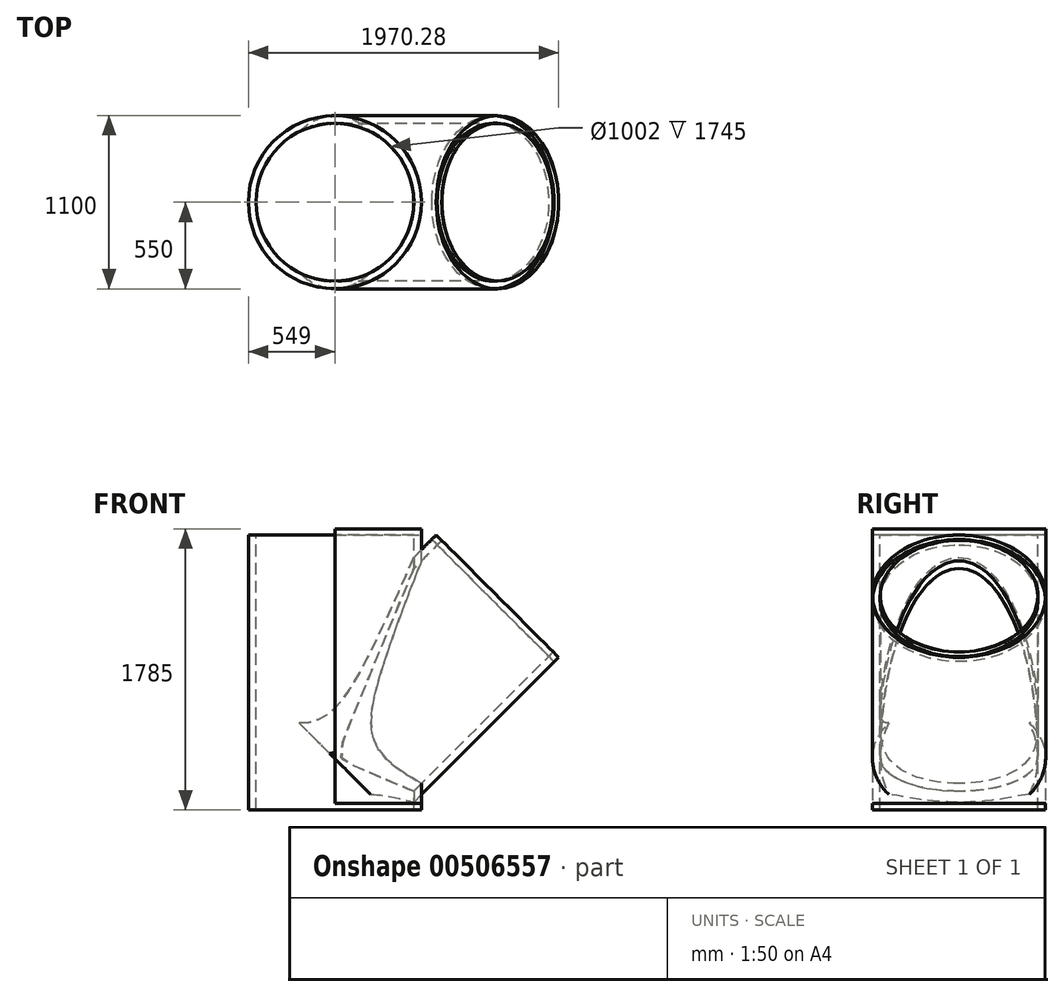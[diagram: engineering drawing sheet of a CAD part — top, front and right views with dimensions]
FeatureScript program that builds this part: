
annotation { "Feature Type Name" : "Feature", "Feature Type Description" : "" }
export const myFeature = defineFeature(function(context is Context, id is Id, definition is map)
    precondition{}
    {
        {
            var Q0;
            Q0=qCreatedBy(makeId("Front.planeOp"),FACE);
            var sketch = newSketch(context, id + "F0", { "sketchPlane" : qUnion([Q0])});
            skLineSegment(sketch, "E0", {"start": v(0, 377.94) * mm, "end": v(0, -525.84) * mm, "construction": true});
            skLineSegment(sketch, "E1", {"start": v(-550, -285) * mm, "end": v(-549, -285) * mm});
            skLineSegment(sketch, "E2", {"start": v(-549, -325) * mm, "end": v(-549, -285) * mm});
            skLineSegment(sketch, "E3", {"start": v(-549, -325) * mm, "end": v(-501, -325) * mm});
            skLineSegment(sketch, "E4", {"start": v(-501, -285) * mm, "end": v(-501, -325) * mm});
            skLineSegment(sketch, "E5", {"start": v(-501, -285) * mm, "end": v(-500, -285) * mm});
            skLineSegment(sketch, "E6", {"start": v(-722.24, 299.16) * mm, "end": v(793.2, -328.56) * mm, "construction": true});
            skLineSegment(sketch, "E7", {"start": v(0, 0) * mm, "end": v(-755.87, 0) * mm, "construction": true});
            skLineSegment(sketch, "E8", {"start": v(0, 0) * mm, "end": v(-598.81, 598.81) * mm, "construction": true});
            skLineSegment(sketch, "E9", {"start": v(-550, -285) * mm, "end": v(-550, 227.82) * mm});
            skLineSegment(sketch, "E10", {"start": v(-500, -285) * mm, "end": v(-500, 207.1) * mm});
            skLineSegment(sketch, "E11", {"start": v(643.47, 1421.28) * mm, "end": v(644.17, 1420.58) * mm});
            skLineSegment(sketch, "E12", {"start": v(615.9, 1392.3) * mm, "end": v(644.17, 1420.58) * mm});
            skLineSegment(sketch, "E13", {"start": v(615.9, 1392.3) * mm, "end": v(649.83, 1358.35) * mm});
            skLineSegment(sketch, "E14", {"start": v(678.12, 1386.64) * mm, "end": v(649.83, 1358.35) * mm});
            skLineSegment(sketch, "E15", {"start": v(678.12, 1386.64) * mm, "end": v(678.82, 1385.93) * mm});
            skLineSegment(sketch, "E16", {"start": v(678.82, 1385.93) * mm, "end": v(-353.55, 353.55) * mm});
            skLineSegment(sketch, "E17", {"start": v(0, 0) * mm, "end": v(275.66, 275.66) * mm, "construction": true});
            skLineSegment(sketch, "E18", {"start": v(-500, 207.1) * mm, "end": v(-500, 1460) * mm});
            skLineSegment(sketch, "E19", {"start": v(-500, 1460) * mm, "end": v(-501, 1460) * mm});
            skLineSegment(sketch, "E20", {"start": v(-501, 1420) * mm, "end": v(-501, 1460) * mm});
            skLineSegment(sketch, "E21", {"start": v(-501, 1420) * mm, "end": v(-549, 1420) * mm});
            skLineSegment(sketch, "E22", {"start": v(-549, 1460) * mm, "end": v(-549, 1420) * mm});
            skLineSegment(sketch, "E23", {"start": v(-549, 1460) * mm, "end": v(-550, 1460) * mm});
            skLineSegment(sketch, "E24", {"start": v(-550, 1460) * mm, "end": v(-550, 227.82) * mm});
            skLineSegment(sketch, "E25.trimOffspring", {"start": v(-388.9, 388.9) * mm, "end": v(643.47, 1421.28) * mm});
            skLineSegment(sketch, "E26", {"start": v(-388.9, 388.9) * mm, "end": v(-353.55, 353.55) * mm});
            skSolve(sketch);
        }
        {
            var Q0;
            Q0=makeQuery(id+"F0.imprint","IMPRINT",FACE,{"disambiguationData":[TD([[makeQuery(id+"F0.imprint","IMPRINT",EDGE,{"derivedFrom":sQuery(id+"F0.wireOp",EDGE,"E1")}),1.0]])]});
            var Q1;
            Q1=sQuery(id+"F0.wireOp",EDGE,"E0");
            revolve(context, id + "F1", {"entities" : qUnion([Q0]), "axis" : qUnion([Q1]), "revolveType" : RevolveType.FULL});
        }
        {
            var Q0;
            Q0=makeQuery(id+"F0.imprint","IMPRINT",FACE,{"disambiguationData":[TD([[makeQuery(id+"F0.imprint","IMPRINT",EDGE,{"derivedFrom":sQuery(id+"F0.wireOp",EDGE,"E11")}),-1.0]])]});
            var Q1;
            Q1=sQuery(id+"F0.wireOp",EDGE,"E17");
            revolve(context, id + "F2", {"entities" : qUnion([Q0]), "axis" : qUnion([Q1]), "revolveType" : RevolveType.FULL});
        }
        {
            var Q0;
            Q0=makeQuery(id+"F2.opRevolve","SWEPT_FACE",FACE,{"disambiguationData":[OSD([sQuery(id+"F0.wireOp",EDGE,"E13")])]});
            var sketch = newSketch(context, id + "F3", { "sketchPlane" : qUnion([Q0])});
            skCircle(sketch, "E27.0", {"center": v(0, 0) * mm, "radius": 500 * mm});
            skSolve(sketch);
        }
        {
            var Q0;
            Q0 = qSketchRegion(id + "F3", true);
            var Q1;
            Q1=makeQuery(id+"F2.opRevolve","SWEPT_FACE",FACE,{"disambiguationData":[OSD([sQuery(id+"F0.wireOp",EDGE,"RudJvVgb-d4Mj-z1rT-Vhq7-xhC1Clk5OM9b")])]});
            extrude(context, id + "F4", {"entities" : qUnion([Q0]), "operationType" : NewBodyOperationType.REMOVE, "oppositeDirection" : true, "depth" : 1420 * mm, "endBoundEntityFace" : qUnion([Q1]), "offsetDistance" : 25 * mm});
        }
        {
            var Q0;
            Q0=makeQuery(id+"F1.opRevolve","SWEPT_FACE",FACE,{"disambiguationData":[OSD([sQuery(id+"F0.wireOp",EDGE,"E3")])]});
            cPlane(context, id + "F5", {"entities" : qUnion([Q0]), "cplaneType" : CPlaneType.OFFSET, "offset" : 500 * mm, "width" : 150 * mm, "height" : 150 * mm});
        }
        {
            var Q0;
            Q0=qCreatedBy(id+"F5.planeOp",FACE);
            var sketch = newSketch(context, id + "F6", { "sketchPlane" : qUnion([Q0])});
            skCircle(sketch, "E28.0", {"center": v(0, 0) * mm, "radius": 501 * mm});
            skCircle(sketch, "E29.0", {"center": v(0, 0) * mm, "radius": 549 * mm, "construction": true});
            skArc(sketch, "E30", {"start": v(0, -549) * mm, "mid": v(-549, 0) * mm, "end": v(0, 549) * mm});
            skLineSegment(sketch, "E31", {"start": v(0, 549) * mm, "end": v(0, 672.32) * mm});
            skArc(sketch, "E32", {"start": v(0, 672.32) * mm, "mid": v(-672.32, 0) * mm, "end": v(0, -672.32) * mm});
            skLineSegment(sketch, "E33", {"start": v(0, -549) * mm, "end": v(0, -672.32) * mm});
            skSolve(sketch);
        }
        {
            var Q0;
            Q0 = qSketchRegion(id + "F6", true);
            extrude(context, id + "F7", {"entities" : qUnion([Q0]), "operationType" : NewBodyOperationType.REMOVE, "oppositeDirection" : true, "depth" : 3000 * mm, "offsetDistance" : 25 * mm});
        }
    });
